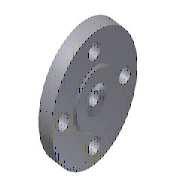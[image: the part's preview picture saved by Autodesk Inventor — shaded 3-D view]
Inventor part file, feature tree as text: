
AUTODESK INVENTOR PART (.ipt)
format: ipt  version: 2024.2 (Build 282272000, 272)  size: 206,848 bytes
history: native  units: mm
features: revolve x1, extrude x1, pattern_circular x1
ambient origin geometry x8: Origin, YZ Plane, XZ Plane, XY Plane, X Axis, Y Axis, Z Axis, Center Point
bodies: Solid1 (feature_tree)
feature tree (3):
  revolve  "Revolution1"  [1 undecoded]
  extrude  "Extrusion1"  Depth=250.0mm
  pattern_circular  "Circular Pattern1"  Angle=90.0deg  [1 undecoded]
note: 2 required parameter values undecoded (feature->parameter linkage not recoverable at this tier; creation-order binding heuristic only, values carry confidence <= 0.55)